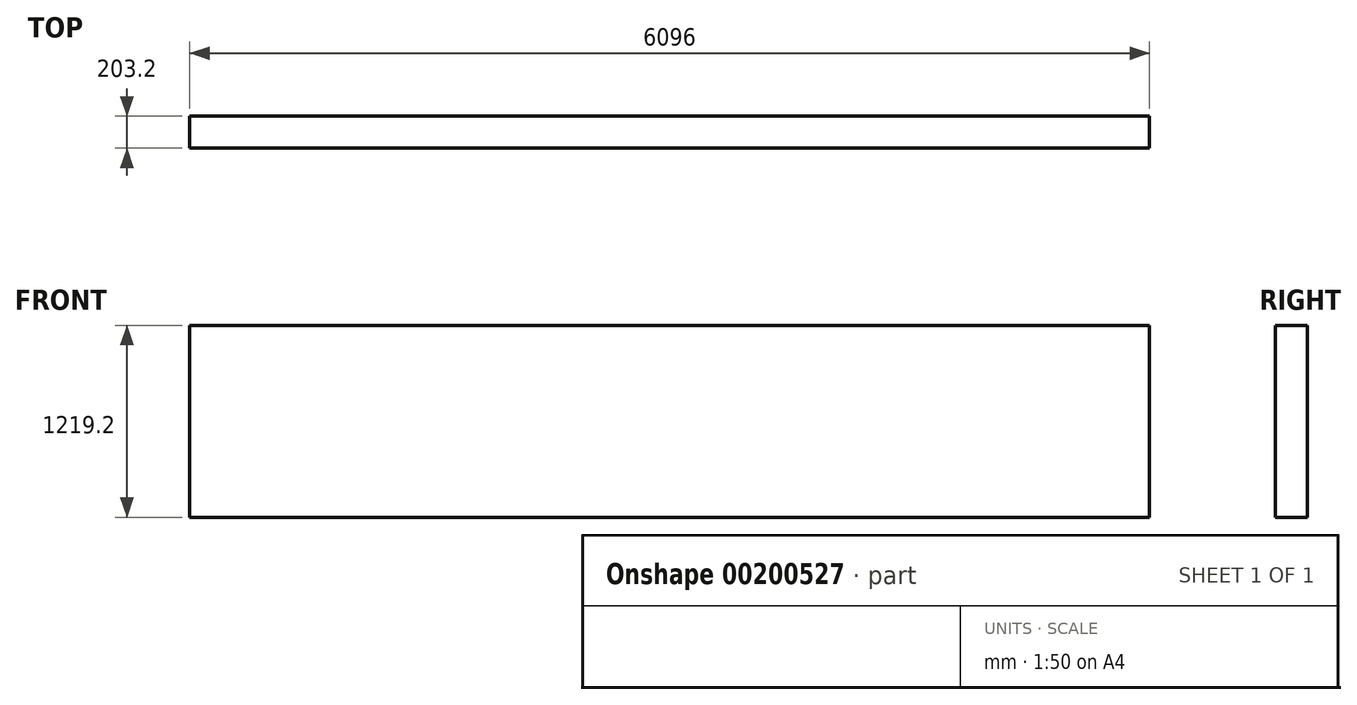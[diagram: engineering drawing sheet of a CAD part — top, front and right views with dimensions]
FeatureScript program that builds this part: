
annotation { "Feature Type Name" : "Feature", "Feature Type Description" : "" }
export const myFeature = defineFeature(function(context is Context, id is Id, definition is map)
    precondition{}
    {
        {
            var Q0;
            Q0=qCreatedBy(makeId("Front.planeOp"),FACE);
            var sketch = newSketch(context, id + "F0", { "sketchPlane" : qUnion([Q0])});
            skLineSegment(sketch, "E0.bottom", {"start": v(-3048, -609.6) * mm, "end": v(3048, -609.6) * mm});
            skLineSegment(sketch, "E0.top", {"start": v(-3048, 609.6) * mm, "end": v(3048, 609.6) * mm});
            skLineSegment(sketch, "E0.left", {"start": v(-3048, -609.6) * mm, "end": v(-3048, 609.6) * mm});
            skLineSegment(sketch, "E0.right", {"start": v(3048, -609.6) * mm, "end": v(3048, 609.6) * mm});
            skSolve(sketch);
        }
        {
            var Q0;
            Q0=makeQuery(id+"F0.imprint","IMPRINT",FACE,{"disambiguationData":[TD([[makeQuery(id+"F0.imprint","IMPRINT",EDGE,{"derivedFrom":sQuery(id+"F0.wireOp",EDGE,"E0.bottom")}),1.0]])]});
            extrude(context, id + "F1", {"entities" : qUnion([Q0]), "depth" : 203.2 * mm, "offsetDistance" : 25.4 * mm});
        }
    });
